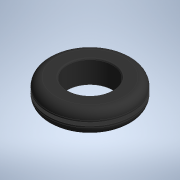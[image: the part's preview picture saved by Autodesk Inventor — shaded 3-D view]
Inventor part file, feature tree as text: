
AUTODESK INVENTOR PART (.ipt)
format: ipt  version: 2020 (Build 240168000, 168)  size: 123,904 bytes
history: native  units: mm (DEFAULTED — no unit token found)
features: fillet x1
ambient origin geometry x8: Origin, YZ Plane, XZ Plane, XY Plane, X Axis, Y Axis, Z Axis, Center Point
bodies: Solid1 (feature_tree)
feature tree (1):
  fillet  "Fillet1"  [1 undecoded]
note: 1 required parameter value undecoded (feature->parameter linkage not recoverable at this tier; creation-order binding heuristic only, values carry confidence <= 0.55)
